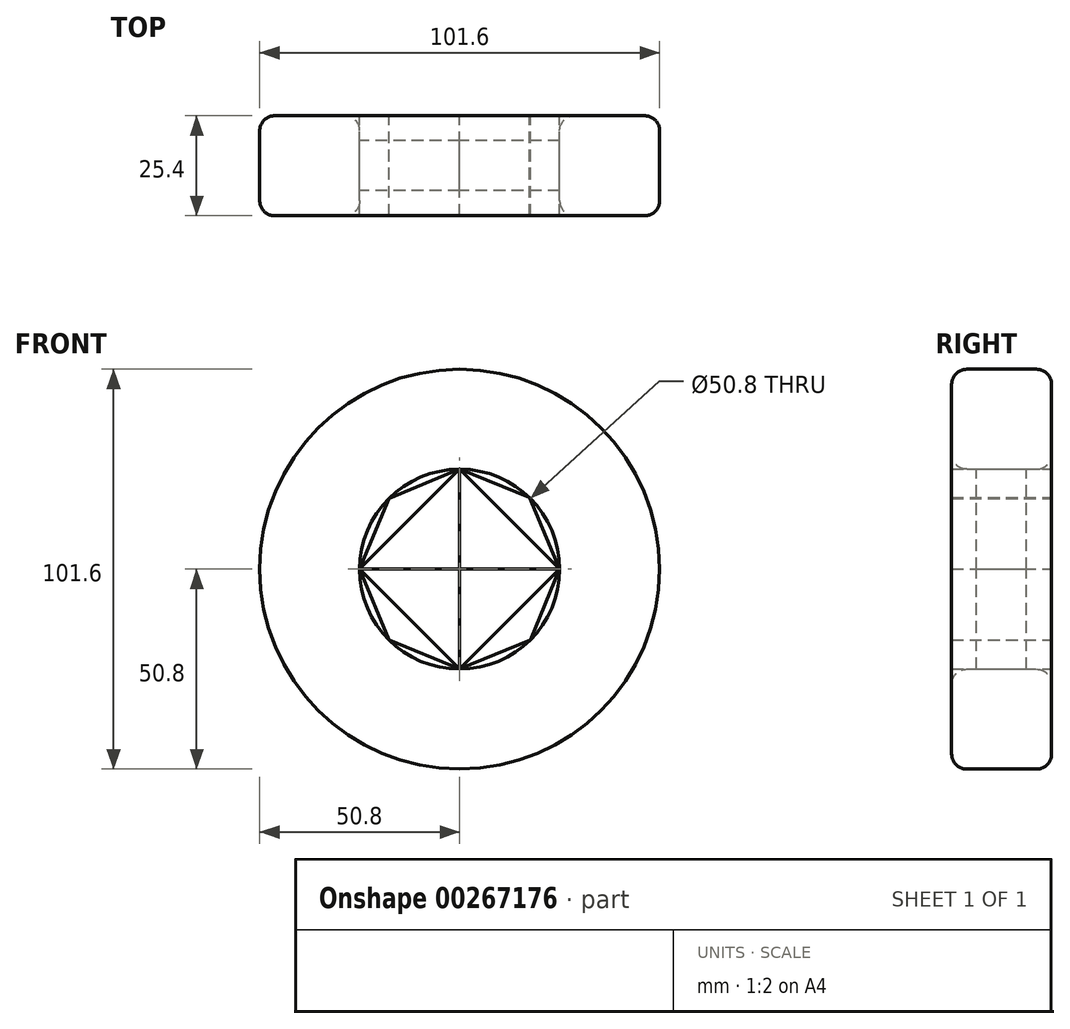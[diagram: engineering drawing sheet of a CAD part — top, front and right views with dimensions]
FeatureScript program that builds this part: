
annotation { "Feature Type Name" : "Feature", "Feature Type Description" : "" }
export const myFeature = defineFeature(function(context is Context, id is Id, definition is map)
    precondition{}
    {
        {
            var Q0;
            Q0=qCreatedBy(makeId("Front.planeOp"),FACE);
            var sketch = newSketch(context, id + "F0", { "sketchPlane" : qUnion([Q0])});
            skCircle(sketch, "E0", {"center": v(0, 0) * mm, "radius": 50.8 * mm});
            skCircle(sketch, "E1", {"center": v(0, 0) * mm, "radius": 25.4 * mm});
            skLineSegment(sketch, "E2", {"start": v(0, 25.4) * mm, "end": v(0, -25.4) * mm});
            skLineSegment(sketch, "E3", {"start": v(0, -25.4) * mm, "end": v(-25.4, 0) * mm});
            skLineSegment(sketch, "E4", {"start": v(-25.4, 0) * mm, "end": v(0, 25.4) * mm});
            skLineSegment(sketch, "E5", {"start": v(25.4, 0) * mm, "end": v(0, 25.4) * mm});
            skLineSegment(sketch, "E6", {"start": v(0, -25.4) * mm, "end": v(25.4, 0) * mm});
            skLineSegment(sketch, "E7", {"start": v(-25.4, 0) * mm, "end": v(25.4, 0) * mm});
            skLineSegment(sketch, "E8", {"start": v(0, 0) * mm, "end": v(12.7, 12.7) * mm});
            skLineSegment(sketch, "E9", {"start": v(0, 0) * mm, "end": v(-12.7, 12.7) * mm});
            skLineSegment(sketch, "E10", {"start": v(-12.7, -12.7) * mm, "end": v(0, 0) * mm});
            skLineSegment(sketch, "E11", {"start": v(12.7, -12.7) * mm, "end": v(0, 0) * mm});
            skLineSegment(sketch, "E12", {"start": v(12.7, -12.7) * mm, "end": v(17.96, -17.96) * mm});
            skLineSegment(sketch, "E13", {"start": v(17.96, -17.96) * mm, "end": v(25.4, 0) * mm});
            skLineSegment(sketch, "E14", {"start": v(17.96, -17.96) * mm, "end": v(0, -25.4) * mm});
            skLineSegment(sketch, "E15", {"start": v(0, -25.4) * mm, "end": v(-17.96, -17.96) * mm});
            skLineSegment(sketch, "E16", {"start": v(-17.96, -17.96) * mm, "end": v(-25.4, 0) * mm});
            skLineSegment(sketch, "E17", {"start": v(0, 25.4) * mm, "end": v(-17.96, 17.96) * mm});
            skLineSegment(sketch, "E18", {"start": v(-17.96, 17.96) * mm, "end": v(-25.4, 0) * mm});
            skLineSegment(sketch, "E19", {"start": v(0, 25.4) * mm, "end": v(17.7, 18.22) * mm});
            skLineSegment(sketch, "E20", {"start": v(17.7, 18.22) * mm, "end": v(25.4, 0) * mm});
            skSolve(sketch);
        }
        {
            var Q0;
            Q0=makeQuery(id+"F0.imprint","IMPRINT",FACE,{"disambiguationData":[TD([[makeQuery(id+"F0.imprint","IMPRINT",EDGE,{"derivedFrom":sQuery(id+"F0.wireOp",EDGE,"E0")}),1.0]])]});
            extrude(context, id + "F1", {"entities" : qUnion([Q0]), "endBound" : BoundingType.SYMMETRIC, "depth" : 25.4 * mm});
        }
        {
            var Q0;
            Q0 = qSketchRegion(id + "F0", true);
            var Q1;
            {var subQ3=sQuery(id+"F0.wireOp",EDGE,"E8");Q1=makeQuery(id+"F0.imprint","IMPRINT",FACE,{"disambiguationData":[TD([[makeQuery(id+"F0.imprint","IMPRINT",EDGE,{"derivedFrom":subQ3}),-1.0]])]});}
            var Q2;
            {var subQ3=sQuery(id+"F0.wireOp",EDGE,"E8");Q2=makeQuery(id+"F0.imprint","IMPRINT",FACE,{"disambiguationData":[TD([[makeQuery(id+"F0.imprint","IMPRINT",EDGE,{"derivedFrom":subQ3}),1.0]])]});}
            var Q3;
            {var subQ3=sQuery(id+"F0.wireOp",EDGE,"E10");Q3=makeQuery(id+"F0.imprint","IMPRINT",FACE,{"disambiguationData":[TD([[makeQuery(id+"F0.imprint","IMPRINT",EDGE,{"derivedFrom":subQ3}),1.0]])]});}
            var Q4;
            {var subQ3=sQuery(id+"F0.wireOp",EDGE,"E10");Q4=makeQuery(id+"F0.imprint","IMPRINT",FACE,{"disambiguationData":[TD([[makeQuery(id+"F0.imprint","IMPRINT",EDGE,{"derivedFrom":subQ3}),-1.0]])]});}
            extrude(context, id + "F2", {"entities" : qUnion([Q0, Q1, Q2, Q3, Q4]), "operationType" : NewBodyOperationType.ADD, "endBound" : BoundingType.SYMMETRIC, "depth" : 12.7 * mm});
        }
        {
            var Q0;
            Q0=makeQuery(id+"F1.opExtrude","CAP_EDGE",EDGE,{"disambiguationData":[OSD([sQuery(id+"F0.wireOp",EDGE,"E0")])],"isStart":true});
            var Q1;
            Q1=makeQuery(id+"F1.opExtrude","CAP_EDGE",EDGE,{"disambiguationData":[OSD([sQuery(id+"F0.wireOp",EDGE,"E0")])],"isStart":false});
            var Q2;
            Q2=makeQuery(id+"F1.opExtrude","CAP_EDGE",EDGE,{"disambiguationData":[OSD([sQuery(id+"F0.wireOp",EDGE,"E1")])],"isStart":false});
            var Q3;
            Q3=makeQuery(id+"F1.opExtrude","CAP_EDGE",EDGE,{"disambiguationData":[OSD([sQuery(id+"F0.wireOp",EDGE,"E1")])],"isStart":true});
            fillet(context, id + "F3", {"entities" : qUnion([Q0, Q1, Q2, Q3]), "radius" : 3.8 * mm, "tangentPropagation" : true, "allowEdgeOverflow" : false});
        }
        {
            var Q0;
            {var subQ2=sQuery(id+"F0.wireOp",EDGE,"E12");Q0=makeQuery(id+"F0.imprint","IMPRINT",FACE,{"disambiguationData":[TD([[makeQuery(id+"F0.imprint","IMPRINT",EDGE,{"derivedFrom":subQ2}),1.0]])]});}
            var Q1;
            {var subQ2=sQuery(id+"F0.wireOp",EDGE,"E12");Q1=makeQuery(id+"F0.imprint","IMPRINT",FACE,{"disambiguationData":[TD([[makeQuery(id+"F0.imprint","IMPRINT",EDGE,{"derivedFrom":subQ2}),-1.0]])]});}
            var Q2;
            {var subQ0=sQuery(id+"F0.wireOp",EDGE,"E15");Q2=makeQuery(id+"F0.imprint","IMPRINT",FACE,{"disambiguationData":[TD([[makeQuery(id+"F0.imprint","IMPRINT",EDGE,{"derivedFrom":subQ0}),-1.0]])]});}
            var Q3;
            {var subQ4=sQuery(id+"F0.wireOp",EDGE,"E17");Q3=makeQuery(id+"F0.imprint","IMPRINT",FACE,{"disambiguationData":[TD([[makeQuery(id+"F0.imprint","IMPRINT",EDGE,{"derivedFrom":subQ4}),1.0]])]});}
            var Q4;
            {var subQ4=sQuery(id+"F0.wireOp",EDGE,"E19");Q4=makeQuery(id+"F0.imprint","IMPRINT",FACE,{"disambiguationData":[TD([[makeQuery(id+"F0.imprint","IMPRINT",EDGE,{"derivedFrom":subQ4}),-1.0]])]});}
            extrude(context, id + "F4", {"entities" : qUnion([Q0, Q1, Q2, Q3, Q4]), "endBound" : BoundingType.SYMMETRIC, "depth" : 25.4 * mm});
        }
    });
